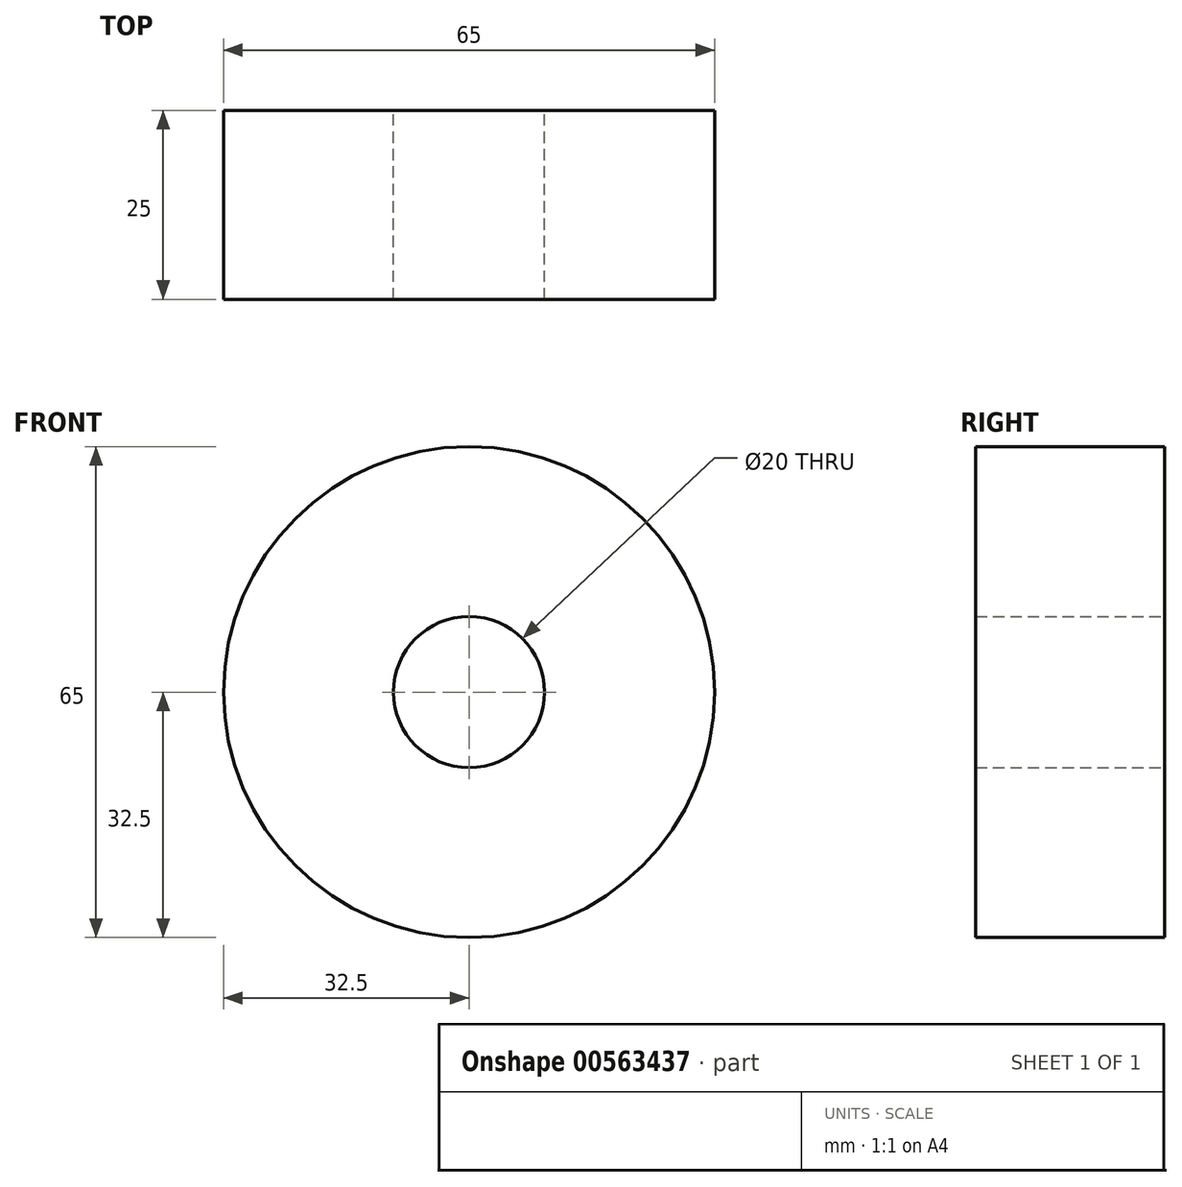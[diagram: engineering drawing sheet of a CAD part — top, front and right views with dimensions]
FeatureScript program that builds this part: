
annotation { "Feature Type Name" : "Feature", "Feature Type Description" : "" }
export const myFeature = defineFeature(function(context is Context, id is Id, definition is map)
    precondition{}
    {
        {
            var Q0;
            Q0=qCreatedBy(makeId("Front.planeOp"),FACE);
            var sketch = newSketch(context, id + "F0", { "sketchPlane" : qUnion([Q0])});
            skCircle(sketch, "E0", {"center": v(0, 0) * mm, "radius": 32.5 * mm});
            skCircle(sketch, "E1", {"center": v(0, 0) * mm, "radius": 10 * mm});
            skLineSegment(sketch, "E2.bottom", {"start": v(-4.49, 60) * mm, "end": v(4.51, 60) * mm, "construction": true});
            skLineSegment(sketch, "E2.top", {"start": v(-4.49, 32.19) * mm, "end": v(4.51, 32.19) * mm});
            skLineSegment(sketch, "E2.left", {"start": v(-4.49, 60) * mm, "end": v(-4.49, 32.19) * mm});
            skLineSegment(sketch, "E2.right", {"start": v(4.51, 60) * mm, "end": v(4.51, 32.19) * mm});
            skSolve(sketch);
        }
        {
            var Q0;
            Q0 = qSketchRegion(id + "F0", true);
            extrude(context, id + "F1", {"entities" : qUnion([Q0]), "depth" : 25 * mm, "offsetDistance" : 25 * mm});
        }
    });
